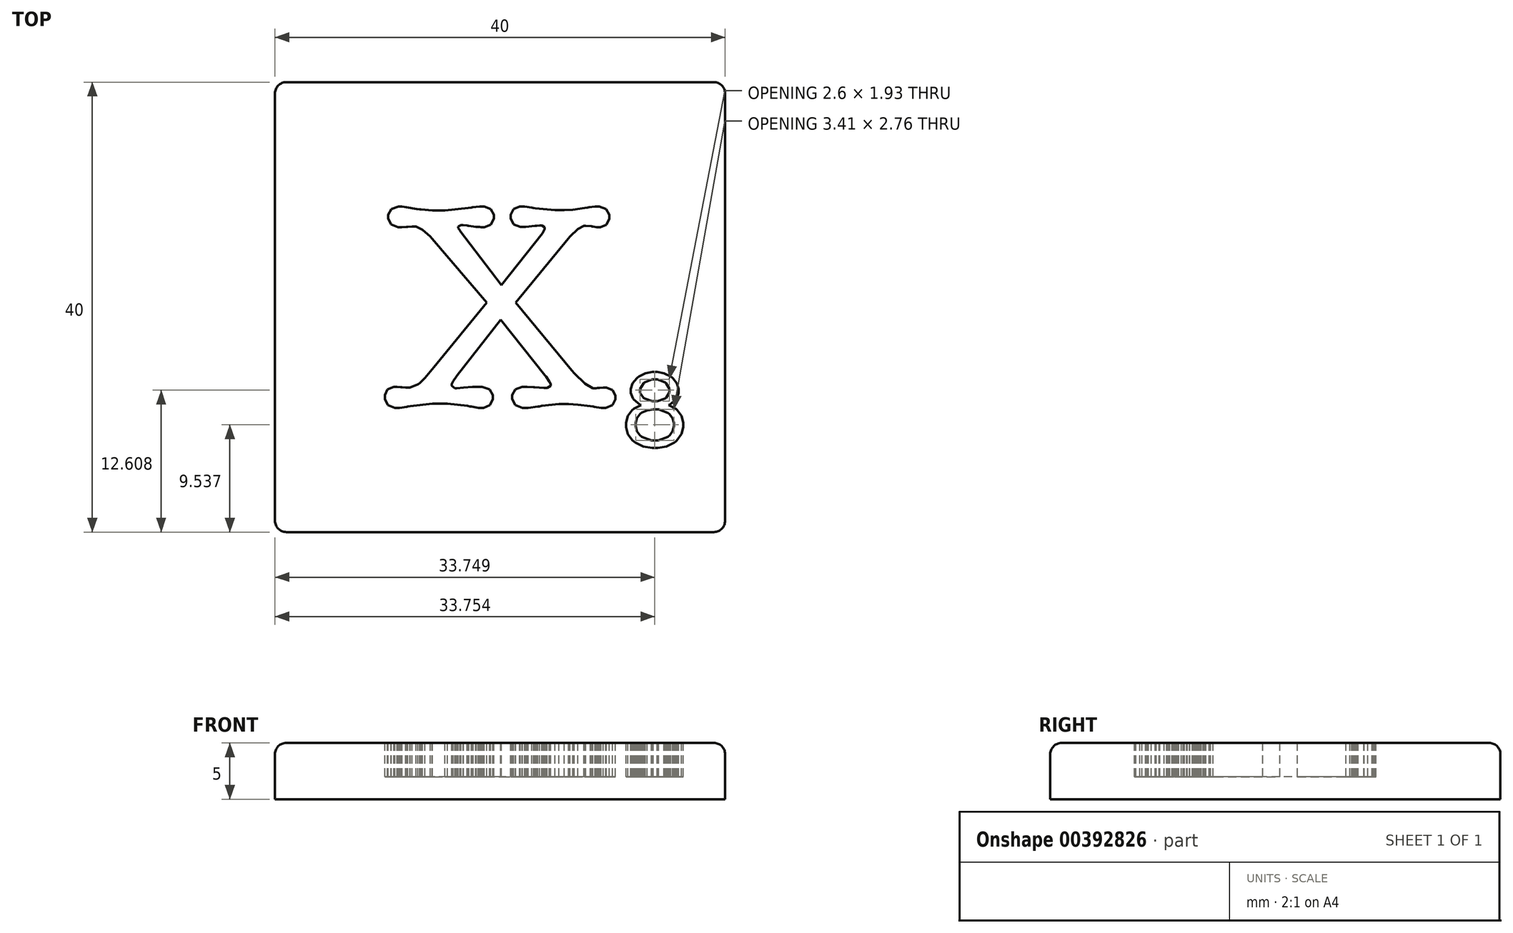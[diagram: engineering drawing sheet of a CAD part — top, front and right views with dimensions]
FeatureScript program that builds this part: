
annotation { "Feature Type Name" : "Feature", "Feature Type Description" : "" }
export const myFeature = defineFeature(function(context is Context, id is Id, definition is map)
    precondition{}
    {
        {
            var Q0;
            Q0=qCreatedBy(makeId("Top.planeOp"),FACE);
            var sketch = newSketch(context, id + "F0", { "sketchPlane" : qUnion([Q0])});
            skLineSegment(sketch, "E0.bottom", {"start": v(20, -20) * mm, "end": v(-20, -20) * mm});
            skLineSegment(sketch, "E0.top", {"start": v(20, 20) * mm, "end": v(-20, 20) * mm});
            skLineSegment(sketch, "E0.left", {"start": v(20, -20) * mm, "end": v(20, 20) * mm});
            skLineSegment(sketch, "E0.right", {"start": v(-20, -20) * mm, "end": v(-20, 20) * mm});
            skPoint(sketch, "E0.middle", {"position": v(0, 0) * mm});
            skSolve(sketch);
        }
        {
            var Q0;
            Q0=makeQuery(id+"F0.imprint","IMPRINT",FACE,{"disambiguationData":[TD([[makeQuery(id+"F0.imprint","IMPRINT",EDGE,{"derivedFrom":sQuery(id+"F0.wireOp",EDGE,"E0.bottom")}),-1.0]])]});
            extrude(context, id + "F1", {"entities" : qUnion([Q0]), "depth" : -5 * mm});
        }
        {
            var Q0;
            Q0=makeQuery(id+"F1.opExtrude","CAP_FACE",FACE,{"disambiguationData":[OSD([sQuery(id+"F0.wireOp",EDGE,"E0.bottom"),sQuery(id+"F0.wireOp",EDGE,"E0.top"),sQuery(id+"F0.wireOp",EDGE,"E0.left"),sQuery(id+"F0.wireOp",EDGE,"E0.right")])],"isStart":true});
            var Q1;
            Q1=makeQuery(id+"F1.opExtrude","SWEPT_EDGE",EDGE,{"disambiguationData":[OSD([sQuery(id+"F0.wireOp",EDGE,"E0.top"),sQuery(id+"F0.wireOp",EDGE,"E0.right")])]});
            var Q2;
            Q2=makeQuery(id+"F1.opExtrude","SWEPT_EDGE",EDGE,{"disambiguationData":[OSD([sQuery(id+"F0.wireOp",EDGE,"E0.top"),sQuery(id+"F0.wireOp",EDGE,"E0.left")])]});
            var Q3;
            Q3=makeQuery(id+"F1.opExtrude","SWEPT_EDGE",EDGE,{"disambiguationData":[OSD([sQuery(id+"F0.wireOp",EDGE,"E0.bottom"),sQuery(id+"F0.wireOp",EDGE,"E0.right")])]});
            var Q4;
            Q4=makeQuery(id+"F1.opExtrude","SWEPT_EDGE",EDGE,{"disambiguationData":[OSD([sQuery(id+"F0.wireOp",EDGE,"E0.bottom"),sQuery(id+"F0.wireOp",EDGE,"E0.left")])]});
            fillet(context, id + "F2", {"entities" : qUnion([Q0, Q1, Q2, Q3, Q4]), "radius" : 1 * mm, "tangentPropagation" : true, "allowEdgeOverflow" : false});
        }
        {
            var Q0;
            Q0=qCreatedBy(makeId("Top.planeOp"),FACE);
            var sketch = newSketch(context, id + "F3", { "sketchPlane" : qUnion([Q0])});
            skLineSegment(sketch, "E1", {"start": v(-5.87, -5.36) * mm, "end": v(-1.2, 0.41) * mm});
            skLineSegment(sketch, "E2", {"start": v(-1.2, 0.41) * mm, "end": v(-6.03, 6.1) * mm});
            skLineSegment(sketch, "E3", {"start": v(-6.03, 6.1) * mm, "end": v(-6.18, 6.28) * mm});
            skLineSegment(sketch, "E4", {"start": v(-6.18, 6.28) * mm, "end": v(-6.9, 6.9) * mm});
            skLineSegment(sketch, "E5", {"start": v(-6.9, 6.9) * mm, "end": v(-7.48, 7.16) * mm});
            skLineSegment(sketch, "E6", {"start": v(-7.48, 7.16) * mm, "end": v(-7.67, 7.16) * mm});
            skLineSegment(sketch, "E7", {"start": v(-7.67, 7.16) * mm, "end": v(-7.82, 7.16) * mm});
            skLineSegment(sketch, "E8", {"start": v(-7.82, 7.16) * mm, "end": v(-8.2, 7.14) * mm});
            skLineSegment(sketch, "E9", {"start": v(-8.2, 7.14) * mm, "end": v(-8.27, 7.13) * mm});
            skLineSegment(sketch, "E10", {"start": v(-8.27, 7.13) * mm, "end": v(-8.33, 7.13) * mm});
            skLineSegment(sketch, "E11", {"start": v(-8.33, 7.13) * mm, "end": v(-8.73, 7.1) * mm});
            skLineSegment(sketch, "E12", {"start": v(-8.73, 7.1) * mm, "end": v(-8.86, 7.1) * mm});
            skLineSegment(sketch, "E13", {"start": v(-8.86, 7.1) * mm, "end": v(-9.07, 7.1) * mm});
            skLineSegment(sketch, "E14", {"start": v(-9.07, 7.1) * mm, "end": v(-9.68, 7.34) * mm});
            skLineSegment(sketch, "E15", {"start": v(-9.68, 7.34) * mm, "end": v(-9.95, 7.88) * mm});
            skLineSegment(sketch, "E16", {"start": v(-9.95, 7.88) * mm, "end": v(-9.95, 8.06) * mm});
            skLineSegment(sketch, "E17", {"start": v(-9.95, 8.06) * mm, "end": v(-9.95, 8.23) * mm});
            skLineSegment(sketch, "E18", {"start": v(-9.95, 8.23) * mm, "end": v(-9.66, 8.73) * mm});
            skLineSegment(sketch, "E19", {"start": v(-9.66, 8.73) * mm, "end": v(-9.02, 8.96) * mm});
            skLineSegment(sketch, "E20", {"start": v(-9.02, 8.96) * mm, "end": v(-8.81, 8.96) * mm});
            skLineSegment(sketch, "E21", {"start": v(-8.81, 8.96) * mm, "end": v(-8.7, 8.96) * mm});
            skLineSegment(sketch, "E22", {"start": v(-8.7, 8.96) * mm, "end": v(-8.33, 8.89) * mm});
            skLineSegment(sketch, "E23", {"start": v(-8.33, 8.89) * mm, "end": v(-7.4, 8.74) * mm});
            skLineSegment(sketch, "E24", {"start": v(-7.4, 8.74) * mm, "end": v(-7.14, 8.7) * mm});
            skLineSegment(sketch, "E25", {"start": v(-7.14, 8.7) * mm, "end": v(-7.02, 8.67) * mm});
            skLineSegment(sketch, "E26", {"start": v(-7.02, 8.67) * mm, "end": v(-6, 8.59) * mm});
            skLineSegment(sketch, "E27", {"start": v(-6, 8.59) * mm, "end": v(-5.66, 8.59) * mm});
            skLineSegment(sketch, "E28", {"start": v(-5.66, 8.59) * mm, "end": v(-4.88, 8.59) * mm});
            skLineSegment(sketch, "E29", {"start": v(-4.88, 8.59) * mm, "end": v(-2.83, 8.8) * mm});
            skLineSegment(sketch, "E30", {"start": v(-2.83, 8.8) * mm, "end": v(-2.54, 8.85) * mm});
            skLineSegment(sketch, "E31", {"start": v(-2.54, 8.85) * mm, "end": v(-2.45, 8.86) * mm});
            skLineSegment(sketch, "E32", {"start": v(-2.45, 8.86) * mm, "end": v(-1.82, 8.93) * mm});
            skLineSegment(sketch, "E33", {"start": v(-1.82, 8.93) * mm, "end": v(-1.61, 8.93) * mm});
            skLineSegment(sketch, "E34", {"start": v(-1.61, 8.93) * mm, "end": v(-1.42, 8.93) * mm});
            skLineSegment(sketch, "E35", {"start": v(-1.42, 8.93) * mm, "end": v(-0.82, 8.7) * mm});
            skLineSegment(sketch, "E36", {"start": v(-0.82, 8.7) * mm, "end": v(-0.56, 8.2) * mm});
            skLineSegment(sketch, "E37", {"start": v(-0.56, 8.2) * mm, "end": v(-0.56, 8.03) * mm});
            skLineSegment(sketch, "E38", {"start": v(-0.56, 8.03) * mm, "end": v(-0.56, 7.86) * mm});
            skLineSegment(sketch, "E39", {"start": v(-0.56, 7.86) * mm, "end": v(-0.82, 7.34) * mm});
            skLineSegment(sketch, "E40", {"start": v(-0.82, 7.34) * mm, "end": v(-1.42, 7.1) * mm});
            skLineSegment(sketch, "E41", {"start": v(-1.42, 7.1) * mm, "end": v(-1.61, 7.1) * mm});
            skLineSegment(sketch, "E42", {"start": v(-1.61, 7.1) * mm, "end": v(-1.68, 7.1) * mm});
            skLineSegment(sketch, "E43", {"start": v(-1.68, 7.1) * mm, "end": v(-1.83, 7.13) * mm});
            skLineSegment(sketch, "E44", {"start": v(-1.83, 7.13) * mm, "end": v(-1.85, 7.13) * mm});
            skLineSegment(sketch, "E45", {"start": v(-1.85, 7.13) * mm, "end": v(-2.1, 7.13) * mm});
            skLineSegment(sketch, "E46", {"start": v(-2.1, 7.13) * mm, "end": v(-2.15, 7.14) * mm});
            skLineSegment(sketch, "E47", {"start": v(-2.15, 7.14) * mm, "end": v(-2.78, 7.23) * mm});
            skLineSegment(sketch, "E48", {"start": v(-2.78, 7.23) * mm, "end": v(-2.84, 7.24) * mm});
            skLineSegment(sketch, "E49", {"start": v(-2.84, 7.24) * mm, "end": v(-2.91, 7.25) * mm});
            skLineSegment(sketch, "E50", {"start": v(-2.91, 7.25) * mm, "end": v(-3.27, 7.29) * mm});
            skLineSegment(sketch, "E51", {"start": v(-3.27, 7.29) * mm, "end": v(-3.39, 7.29) * mm});
            skLineSegment(sketch, "E52", {"start": v(-3.39, 7.29) * mm, "end": v(-3.47, 7.29) * mm});
            skLineSegment(sketch, "E53", {"start": v(-3.47, 7.29) * mm, "end": v(-3.7, 7.15) * mm});
            skLineSegment(sketch, "E54", {"start": v(-3.7, 7.15) * mm, "end": v(-3.7, 7.1) * mm});
            skLineSegment(sketch, "E55", {"start": v(-3.7, 7.1) * mm, "end": v(-3.7, 7.03) * mm});
            skLineSegment(sketch, "E56", {"start": v(-3.7, 7.03) * mm, "end": v(-3.57, 6.82) * mm});
            skLineSegment(sketch, "E57", {"start": v(-3.57, 6.82) * mm, "end": v(-3.55, 6.79) * mm});
            skLineSegment(sketch, "E58", {"start": v(-3.55, 6.79) * mm, "end": v(0.13, 1.97) * mm});
            skLineSegment(sketch, "E59", {"start": v(0.13, 1.97) * mm, "end": v(3.76, 6.57) * mm});
            skLineSegment(sketch, "E60", {"start": v(3.76, 6.57) * mm, "end": v(3.8, 6.62) * mm});
            skLineSegment(sketch, "E61", {"start": v(3.8, 6.62) * mm, "end": v(3.97, 6.94) * mm});
            skLineSegment(sketch, "E62", {"start": v(3.97, 6.94) * mm, "end": v(3.97, 7.05) * mm});
            skLineSegment(sketch, "E63", {"start": v(3.97, 7.05) * mm, "end": v(3.97, 7.1) * mm});
            skLineSegment(sketch, "E64", {"start": v(3.97, 7.1) * mm, "end": v(3.71, 7.26) * mm});
            skLineSegment(sketch, "E65", {"start": v(3.71, 7.26) * mm, "end": v(3.62, 7.26) * mm});
            skLineSegment(sketch, "E66", {"start": v(3.62, 7.26) * mm, "end": v(3.53, 7.26) * mm});
            skLineSegment(sketch, "E67", {"start": v(3.53, 7.26) * mm, "end": v(3.26, 7.24) * mm});
            skLineSegment(sketch, "E68", {"start": v(3.26, 7.24) * mm, "end": v(3.23, 7.24) * mm});
            skLineSegment(sketch, "E69", {"start": v(3.23, 7.24) * mm, "end": v(3.1, 7.22) * mm});
            skLineSegment(sketch, "E70", {"start": v(3.1, 7.22) * mm, "end": v(2.28, 7.13) * mm});
            skLineSegment(sketch, "E71", {"start": v(2.28, 7.13) * mm, "end": v(2, 7.13) * mm});
            skLineSegment(sketch, "E72", {"start": v(2, 7.13) * mm, "end": v(1.81, 7.13) * mm});
            skLineSegment(sketch, "E73", {"start": v(1.81, 7.13) * mm, "end": v(1.22, 7.36) * mm});
            skLineSegment(sketch, "E74", {"start": v(1.22, 7.36) * mm, "end": v(0.95, 7.88) * mm});
            skLineSegment(sketch, "E75", {"start": v(0.95, 7.88) * mm, "end": v(0.95, 8.06) * mm});
            skLineSegment(sketch, "E76", {"start": v(0.95, 8.06) * mm, "end": v(0.95, 8.22) * mm});
            skLineSegment(sketch, "E77", {"start": v(0.95, 8.22) * mm, "end": v(1.2, 8.71) * mm});
            skLineSegment(sketch, "E78", {"start": v(1.2, 8.71) * mm, "end": v(1.75, 8.93) * mm});
            skLineSegment(sketch, "E79", {"start": v(1.75, 8.93) * mm, "end": v(1.93, 8.93) * mm});
            skLineSegment(sketch, "E80", {"start": v(1.93, 8.93) * mm, "end": v(2.18, 8.93) * mm});
            skLineSegment(sketch, "E81", {"start": v(2.18, 8.93) * mm, "end": v(2.83, 8.84) * mm});
            skLineSegment(sketch, "E82", {"start": v(2.83, 8.84) * mm, "end": v(2.94, 8.82) * mm});
            skLineSegment(sketch, "E83", {"start": v(2.94, 8.82) * mm, "end": v(3.14, 8.79) * mm});
            skLineSegment(sketch, "E84", {"start": v(3.14, 8.79) * mm, "end": v(4.9, 8.61) * mm});
            skLineSegment(sketch, "E85", {"start": v(4.9, 8.61) * mm, "end": v(5.48, 8.61) * mm});
            skLineSegment(sketch, "E86", {"start": v(5.48, 8.61) * mm, "end": v(5.72, 8.61) * mm});
            skLineSegment(sketch, "E87", {"start": v(5.72, 8.61) * mm, "end": v(6.46, 8.67) * mm});
            skLineSegment(sketch, "E88", {"start": v(6.46, 8.67) * mm, "end": v(7.53, 8.81) * mm});
            skLineSegment(sketch, "E89", {"start": v(7.53, 8.81) * mm, "end": v(7.78, 8.85) * mm});
            skLineSegment(sketch, "E90", {"start": v(7.78, 8.85) * mm, "end": v(7.89, 8.87) * mm});
            skLineSegment(sketch, "E91", {"start": v(7.89, 8.87) * mm, "end": v(8.44, 8.96) * mm});
            skLineSegment(sketch, "E92", {"start": v(8.44, 8.96) * mm, "end": v(8.62, 8.96) * mm});
            skLineSegment(sketch, "E93", {"start": v(8.62, 8.96) * mm, "end": v(8.83, 8.96) * mm});
            skLineSegment(sketch, "E94", {"start": v(8.83, 8.96) * mm, "end": v(9.44, 8.72) * mm});
            skLineSegment(sketch, "E95", {"start": v(9.44, 8.72) * mm, "end": v(9.71, 8.2) * mm});
            skLineSegment(sketch, "E96", {"start": v(9.71, 8.2) * mm, "end": v(9.71, 8.03) * mm});
            skLineSegment(sketch, "E97", {"start": v(9.71, 8.03) * mm, "end": v(9.71, 7.86) * mm});
            skLineSegment(sketch, "E98", {"start": v(9.71, 7.86) * mm, "end": v(9.47, 7.34) * mm});
            skLineSegment(sketch, "E99", {"start": v(9.47, 7.34) * mm, "end": v(8.91, 7.1) * mm});
            skLineSegment(sketch, "E100", {"start": v(8.91, 7.1) * mm, "end": v(8.73, 7.1) * mm});
            skLineSegment(sketch, "E101", {"start": v(8.73, 7.1) * mm, "end": v(8.6, 7.1) * mm});
            skLineSegment(sketch, "E102", {"start": v(8.6, 7.1) * mm, "end": v(8.24, 7.16) * mm});
            skLineSegment(sketch, "E103", {"start": v(8.24, 7.16) * mm, "end": v(8.18, 7.17) * mm});
            skLineSegment(sketch, "E104", {"start": v(8.18, 7.17) * mm, "end": v(8.11, 7.18) * mm});
            skLineSegment(sketch, "E105", {"start": v(8.11, 7.18) * mm, "end": v(7.62, 7.24) * mm});
            skLineSegment(sketch, "E106", {"start": v(7.62, 7.24) * mm, "end": v(7.44, 7.24) * mm});
            skLineSegment(sketch, "E107", {"start": v(7.44, 7.24) * mm, "end": v(6.91, 6.95) * mm});
            skLineSegment(sketch, "E108", {"start": v(6.91, 6.95) * mm, "end": v(6.21, 6.29) * mm});
            skLineSegment(sketch, "E109", {"start": v(6.21, 6.29) * mm, "end": v(6.06, 6.1) * mm});
            skLineSegment(sketch, "E110", {"start": v(6.06, 6.1) * mm, "end": v(1.4, 0.41) * mm});
            skLineSegment(sketch, "E111", {"start": v(1.4, 0.41) * mm, "end": v(6.38, -5.62) * mm});
            skLineSegment(sketch, "E112", {"start": v(6.38, -5.62) * mm, "end": v(6.6, -5.89) * mm});
            skLineSegment(sketch, "E113", {"start": v(6.6, -5.89) * mm, "end": v(7.55, -6.81) * mm});
            skLineSegment(sketch, "E114", {"start": v(7.55, -6.81) * mm, "end": v(8.26, -7.2) * mm});
            skLineSegment(sketch, "E115", {"start": v(8.26, -7.2) * mm, "end": v(8.5, -7.2) * mm});
            skLineSegment(sketch, "E116", {"start": v(8.5, -7.2) * mm, "end": v(8.54, -7.2) * mm});
            skLineSegment(sketch, "E117", {"start": v(8.54, -7.2) * mm, "end": v(8.66, -7.19) * mm});
            skLineSegment(sketch, "E118", {"start": v(8.66, -7.19) * mm, "end": v(8.68, -7.18) * mm});
            skLineSegment(sketch, "E119", {"start": v(8.68, -7.18) * mm, "end": v(8.84, -7.18) * mm});
            skLineSegment(sketch, "E120", {"start": v(8.84, -7.18) * mm, "end": v(8.86, -7.18) * mm});
            skLineSegment(sketch, "E121", {"start": v(8.86, -7.18) * mm, "end": v(9.16, -7.16) * mm});
            skLineSegment(sketch, "E122", {"start": v(9.16, -7.16) * mm, "end": v(9.26, -7.16) * mm});
            skLineSegment(sketch, "E123", {"start": v(9.26, -7.16) * mm, "end": v(9.44, -7.16) * mm});
            skLineSegment(sketch, "E124", {"start": v(9.44, -7.16) * mm, "end": v(10, -7.37) * mm});
            skLineSegment(sketch, "E125", {"start": v(10, -7.37) * mm, "end": v(10.24, -7.87) * mm});
            skLineSegment(sketch, "E126", {"start": v(10.24, -7.87) * mm, "end": v(10.24, -8.03) * mm});
            skLineSegment(sketch, "E127", {"start": v(10.24, -8.03) * mm, "end": v(10.24, -8.2) * mm});
            skLineSegment(sketch, "E128", {"start": v(10.24, -8.2) * mm, "end": v(9.98, -8.72) * mm});
            skLineSegment(sketch, "E129", {"start": v(9.98, -8.72) * mm, "end": v(9.4, -8.96) * mm});
            skLineSegment(sketch, "E130", {"start": v(9.4, -8.96) * mm, "end": v(9.2, -8.96) * mm});
            skLineSegment(sketch, "E131", {"start": v(9.2, -8.96) * mm, "end": v(8.98, -8.96) * mm});
            skLineSegment(sketch, "E132", {"start": v(8.98, -8.96) * mm, "end": v(8.4, -8.87) * mm});
            skLineSegment(sketch, "E133", {"start": v(8.4, -8.87) * mm, "end": v(8.28, -8.85) * mm});
            skLineSegment(sketch, "E134", {"start": v(8.28, -8.85) * mm, "end": v(8.03, -8.8) * mm});
            skLineSegment(sketch, "E135", {"start": v(8.03, -8.8) * mm, "end": v(6.91, -8.67) * mm});
            skLineSegment(sketch, "E136", {"start": v(6.91, -8.67) * mm, "end": v(6.1, -8.61) * mm});
            skLineSegment(sketch, "E137", {"start": v(6.1, -8.61) * mm, "end": v(5.82, -8.61) * mm});
            skLineSegment(sketch, "E138", {"start": v(5.82, -8.61) * mm, "end": v(5.24, -8.61) * mm});
            skLineSegment(sketch, "E139", {"start": v(5.24, -8.61) * mm, "end": v(3.7, -8.79) * mm});
            skLineSegment(sketch, "E140", {"start": v(3.7, -8.79) * mm, "end": v(3.5, -8.82) * mm});
            skLineSegment(sketch, "E141", {"start": v(3.5, -8.82) * mm, "end": v(3.36, -8.85) * mm});
            skLineSegment(sketch, "E142", {"start": v(3.36, -8.85) * mm, "end": v(2.5, -8.96) * mm});
            skLineSegment(sketch, "E143", {"start": v(2.5, -8.96) * mm, "end": v(2.22, -8.96) * mm});
            skLineSegment(sketch, "E144", {"start": v(2.22, -8.96) * mm, "end": v(2, -8.96) * mm});
            skLineSegment(sketch, "E145", {"start": v(2, -8.96) * mm, "end": v(1.37, -8.72) * mm});
            skLineSegment(sketch, "E146", {"start": v(1.37, -8.72) * mm, "end": v(1.08, -8.18) * mm});
            skLineSegment(sketch, "E147", {"start": v(1.08, -8.18) * mm, "end": v(1.08, -8) * mm});
            skLineSegment(sketch, "E148", {"start": v(1.08, -8) * mm, "end": v(1.08, -7.83) * mm});
            skLineSegment(sketch, "E149", {"start": v(1.08, -7.83) * mm, "end": v(1.36, -7.33) * mm});
            skLineSegment(sketch, "E150", {"start": v(1.36, -7.33) * mm, "end": v(1.97, -7.1) * mm});
            skLineSegment(sketch, "E151", {"start": v(1.97, -7.1) * mm, "end": v(2.17, -7.1) * mm});
            skLineSegment(sketch, "E152", {"start": v(2.17, -7.1) * mm, "end": v(2.4, -7.1) * mm});
            skLineSegment(sketch, "E153", {"start": v(2.4, -7.1) * mm, "end": v(3, -7.12) * mm});
            skLineSegment(sketch, "E154", {"start": v(3, -7.12) * mm, "end": v(3.07, -7.13) * mm});
            skLineSegment(sketch, "E155", {"start": v(3.07, -7.13) * mm, "end": v(3.89, -7.18) * mm});
            skLineSegment(sketch, "E156", {"start": v(3.89, -7.18) * mm, "end": v(4.07, -7.18) * mm});
            skLineSegment(sketch, "E157", {"start": v(4.07, -7.18) * mm, "end": v(4.18, -7.18) * mm});
            skLineSegment(sketch, "E158", {"start": v(4.18, -7.18) * mm, "end": v(4.5, -6.99) * mm});
            skLineSegment(sketch, "E159", {"start": v(4.5, -6.99) * mm, "end": v(4.5, -6.92) * mm});
            skLineSegment(sketch, "E160", {"start": v(4.5, -6.92) * mm, "end": v(4.5, -6.84) * mm});
            skLineSegment(sketch, "E161", {"start": v(4.5, -6.84) * mm, "end": v(4.37, -6.6) * mm});
            skLineSegment(sketch, "E162", {"start": v(4.37, -6.6) * mm, "end": v(4.08, -6.18) * mm});
            skLineSegment(sketch, "E163", {"start": v(4.08, -6.18) * mm, "end": v(4, -6.07) * mm});
            skLineSegment(sketch, "E164", {"start": v(4, -6.07) * mm, "end": v(0.05, -1.12) * mm});
            skLineSegment(sketch, "E165", {"start": v(0.05, -1.12) * mm, "end": v(-3.81, -6.07) * mm});
            skLineSegment(sketch, "E166", {"start": v(-3.81, -6.07) * mm, "end": v(-3.9, -6.17) * mm});
            skLineSegment(sketch, "E167", {"start": v(-3.9, -6.17) * mm, "end": v(-4.17, -6.59) * mm});
            skLineSegment(sketch, "E168", {"start": v(-4.17, -6.59) * mm, "end": v(-4.29, -6.84) * mm});
            skLineSegment(sketch, "E169", {"start": v(-4.29, -6.84) * mm, "end": v(-4.29, -6.92) * mm});
            skLineSegment(sketch, "E170", {"start": v(-4.29, -6.92) * mm, "end": v(-4.29, -7) * mm});
            skLineSegment(sketch, "E171", {"start": v(-4.29, -7) * mm, "end": v(-4, -7.2) * mm});
            skLineSegment(sketch, "E172", {"start": v(-4, -7.2) * mm, "end": v(-3.92, -7.2) * mm});
            skLineSegment(sketch, "E173", {"start": v(-3.92, -7.2) * mm, "end": v(-3.86, -7.2) * mm});
            skLineSegment(sketch, "E174", {"start": v(-3.86, -7.2) * mm, "end": v(-3.25, -7.16) * mm});
            skLineSegment(sketch, "E175", {"start": v(-3.25, -7.16) * mm, "end": v(-2.46, -7.1) * mm});
            skLineSegment(sketch, "E176", {"start": v(-2.46, -7.1) * mm, "end": v(-2.4, -7.1) * mm});
            skLineSegment(sketch, "E177", {"start": v(-2.4, -7.1) * mm, "end": v(-1.95, -7.08) * mm});
            skLineSegment(sketch, "E178", {"start": v(-1.95, -7.08) * mm, "end": v(-1.8, -7.08) * mm});
            skLineSegment(sketch, "E179", {"start": v(-1.8, -7.08) * mm, "end": v(-1.58, -7.08) * mm});
            skLineSegment(sketch, "E180", {"start": v(-1.58, -7.08) * mm, "end": v(-0.93, -7.3) * mm});
            skLineSegment(sketch, "E181", {"start": v(-0.93, -7.3) * mm, "end": v(-0.64, -7.83) * mm});
            skLineSegment(sketch, "E182", {"start": v(-0.64, -7.83) * mm, "end": v(-0.64, -8) * mm});
            skLineSegment(sketch, "E183", {"start": v(-0.64, -8) * mm, "end": v(-0.64, -8.18) * mm});
            skLineSegment(sketch, "E184", {"start": v(-0.64, -8.18) * mm, "end": v(-0.89, -8.72) * mm});
            skLineSegment(sketch, "E185", {"start": v(-0.89, -8.72) * mm, "end": v(-1.45, -8.96) * mm});
            skLineSegment(sketch, "E186", {"start": v(-1.45, -8.96) * mm, "end": v(-1.64, -8.96) * mm});
            skLineSegment(sketch, "E187", {"start": v(-1.64, -8.96) * mm, "end": v(-1.9, -8.96) * mm});
            skLineSegment(sketch, "E188", {"start": v(-1.9, -8.96) * mm, "end": v(-2.55, -8.85) * mm});
            skLineSegment(sketch, "E189", {"start": v(-2.55, -8.85) * mm, "end": v(-2.67, -8.82) * mm});
            skLineSegment(sketch, "E190", {"start": v(-2.67, -8.82) * mm, "end": v(-2.89, -8.78) * mm});
            skLineSegment(sketch, "E191", {"start": v(-2.89, -8.78) * mm, "end": v(-4.67, -8.59) * mm});
            skLineSegment(sketch, "E192", {"start": v(-4.67, -8.59) * mm, "end": v(-5.27, -8.59) * mm});
            skLineSegment(sketch, "E193", {"start": v(-5.27, -8.59) * mm, "end": v(-6, -8.59) * mm});
            skLineSegment(sketch, "E194", {"start": v(-6, -8.59) * mm, "end": v(-7.96, -8.8) * mm});
            skLineSegment(sketch, "E195", {"start": v(-7.96, -8.8) * mm, "end": v(-8.2, -8.85) * mm});
            skLineSegment(sketch, "E196", {"start": v(-8.2, -8.85) * mm, "end": v(-8.3, -8.87) * mm});
            skLineSegment(sketch, "E197", {"start": v(-8.3, -8.87) * mm, "end": v(-8.92, -8.96) * mm});
            skLineSegment(sketch, "E198", {"start": v(-8.92, -8.96) * mm, "end": v(-9.13, -8.96) * mm});
            skLineSegment(sketch, "E199", {"start": v(-9.13, -8.96) * mm, "end": v(-9.34, -8.96) * mm});
            skLineSegment(sketch, "E200", {"start": v(-9.34, -8.96) * mm, "end": v(-9.96, -8.72) * mm});
            skLineSegment(sketch, "E201", {"start": v(-9.96, -8.72) * mm, "end": v(-10.24, -8.18) * mm});
            skLineSegment(sketch, "E202", {"start": v(-10.24, -8.18) * mm, "end": v(-10.24, -8) * mm});
            skLineSegment(sketch, "E203", {"start": v(-10.24, -8) * mm, "end": v(-10.24, -7.83) * mm});
            skLineSegment(sketch, "E204", {"start": v(-10.24, -7.83) * mm, "end": v(-10, -7.3) * mm});
            skLineSegment(sketch, "E205", {"start": v(-10, -7.3) * mm, "end": v(-9.45, -7.08) * mm});
            skLineSegment(sketch, "E206", {"start": v(-9.45, -7.08) * mm, "end": v(-9.26, -7.08) * mm});
            skLineSegment(sketch, "E207", {"start": v(-9.26, -7.08) * mm, "end": v(-9.14, -7.08) * mm});
            skLineSegment(sketch, "E208", {"start": v(-9.14, -7.08) * mm, "end": v(-8.83, -7.11) * mm});
            skLineSegment(sketch, "E209", {"start": v(-8.83, -7.11) * mm, "end": v(-8.77, -7.12) * mm});
            skLineSegment(sketch, "E210", {"start": v(-8.77, -7.12) * mm, "end": v(-8.72, -7.12) * mm});
            skLineSegment(sketch, "E211", {"start": v(-8.72, -7.12) * mm, "end": v(-8.4, -7.16) * mm});
            skLineSegment(sketch, "E212", {"start": v(-8.4, -7.16) * mm, "end": v(-8.28, -7.16) * mm});
            skLineSegment(sketch, "E213", {"start": v(-8.28, -7.16) * mm, "end": v(-8.02, -7.16) * mm});
            skLineSegment(sketch, "E214", {"start": v(-8.02, -7.16) * mm, "end": v(-7.3, -6.88) * mm});
            skLineSegment(sketch, "E215", {"start": v(-7.3, -6.88) * mm, "end": v(-7.24, -6.83) * mm});
            skLineSegment(sketch, "E216", {"start": v(-7.24, -6.83) * mm, "end": v(-7.17, -6.77) * mm});
            skLineSegment(sketch, "E217", {"start": v(-7.17, -6.77) * mm, "end": v(-6.68, -6.3) * mm});
            skLineSegment(sketch, "E218", {"start": v(-6.68, -6.3) * mm, "end": v(-6.03, -5.55) * mm});
            skLineSegment(sketch, "E219", {"start": v(-6.03, -5.55) * mm, "end": v(-5.87, -5.36) * mm});
            skSolve(sketch);
        }
        {
            var Q0;
            Q0=qCreatedBy(makeId("Top.planeOp"),FACE);
            var sketch = newSketch(context, id + "F4", { "sketchPlane" : qUnion([Q0])});
            skLineSegment(sketch, "E220", {"start": v(11.87, -9.06) * mm, "end": v(11.9, -9.03) * mm});
            skLineSegment(sketch, "E221", {"start": v(11.9, -9.03) * mm, "end": v(12.46, -8.74) * mm});
            skLineSegment(sketch, "E222", {"start": v(12.46, -8.74) * mm, "end": v(12.53, -8.72) * mm});
            skLineSegment(sketch, "E223", {"start": v(12.53, -8.72) * mm, "end": v(12.45, -8.67) * mm});
            skLineSegment(sketch, "E224", {"start": v(12.45, -8.67) * mm, "end": v(11.85, -8.2) * mm});
            skLineSegment(sketch, "E225", {"start": v(11.85, -8.2) * mm, "end": v(11.82, -8.15) * mm});
            skLineSegment(sketch, "E226", {"start": v(11.82, -8.15) * mm, "end": v(11.79, -8.1) * mm});
            skLineSegment(sketch, "E227", {"start": v(11.79, -8.1) * mm, "end": v(11.63, -7.62) * mm});
            skLineSegment(sketch, "E228", {"start": v(11.63, -7.62) * mm, "end": v(11.63, -7.45) * mm});
            skLineSegment(sketch, "E229", {"start": v(11.63, -7.45) * mm, "end": v(11.63, -7.29) * mm});
            skLineSegment(sketch, "E230", {"start": v(11.63, -7.29) * mm, "end": v(11.78, -6.79) * mm});
            skLineSegment(sketch, "E231", {"start": v(11.78, -6.79) * mm, "end": v(12.14, -6.32) * mm});
            skLineSegment(sketch, "E232", {"start": v(12.14, -6.32) * mm, "end": v(12.24, -6.24) * mm});
            skLineSegment(sketch, "E233", {"start": v(12.24, -6.24) * mm, "end": v(12.35, -6.16) * mm});
            skLineSegment(sketch, "E234", {"start": v(12.35, -6.16) * mm, "end": v(12.93, -5.87) * mm});
            skLineSegment(sketch, "E235", {"start": v(12.93, -5.87) * mm, "end": v(13.55, -5.75) * mm});
            skLineSegment(sketch, "E236", {"start": v(13.55, -5.75) * mm, "end": v(13.75, -5.75) * mm});
            skLineSegment(sketch, "E237", {"start": v(13.75, -5.75) * mm, "end": v(13.96, -5.75) * mm});
            skLineSegment(sketch, "E238", {"start": v(13.96, -5.75) * mm, "end": v(14.58, -5.87) * mm});
            skLineSegment(sketch, "E239", {"start": v(14.58, -5.87) * mm, "end": v(15.16, -6.16) * mm});
            skLineSegment(sketch, "E240", {"start": v(15.16, -6.16) * mm, "end": v(15.26, -6.24) * mm});
            skLineSegment(sketch, "E241", {"start": v(15.26, -6.24) * mm, "end": v(15.37, -6.32) * mm});
            skLineSegment(sketch, "E242", {"start": v(15.37, -6.32) * mm, "end": v(15.72, -6.79) * mm});
            skLineSegment(sketch, "E243", {"start": v(15.72, -6.79) * mm, "end": v(15.88, -7.29) * mm});
            skLineSegment(sketch, "E244", {"start": v(15.88, -7.29) * mm, "end": v(15.88, -7.45) * mm});
            skLineSegment(sketch, "E245", {"start": v(15.88, -7.45) * mm, "end": v(15.88, -7.63) * mm});
            skLineSegment(sketch, "E246", {"start": v(15.88, -7.63) * mm, "end": v(15.72, -8.1) * mm});
            skLineSegment(sketch, "E247", {"start": v(15.72, -8.1) * mm, "end": v(15.68, -8.15) * mm});
            skLineSegment(sketch, "E248", {"start": v(15.68, -8.15) * mm, "end": v(15.65, -8.2) * mm});
            skLineSegment(sketch, "E249", {"start": v(15.65, -8.2) * mm, "end": v(15.06, -8.67) * mm});
            skLineSegment(sketch, "E250", {"start": v(15.06, -8.67) * mm, "end": v(14.97, -8.72) * mm});
            skLineSegment(sketch, "E251", {"start": v(14.97, -8.72) * mm, "end": v(15.04, -8.74) * mm});
            skLineSegment(sketch, "E252", {"start": v(15.04, -8.74) * mm, "end": v(15.59, -9.03) * mm});
            skLineSegment(sketch, "E253", {"start": v(15.59, -9.03) * mm, "end": v(15.63, -9.06) * mm});
            skLineSegment(sketch, "E254", {"start": v(15.63, -9.06) * mm, "end": v(15.74, -9.15) * mm});
            skLineSegment(sketch, "E255", {"start": v(15.74, -9.15) * mm, "end": v(16.13, -9.67) * mm});
            skLineSegment(sketch, "E256", {"start": v(16.13, -9.67) * mm, "end": v(16.3, -10.26) * mm});
            skLineSegment(sketch, "E257", {"start": v(16.3, -10.26) * mm, "end": v(16.3, -10.46) * mm});
            skLineSegment(sketch, "E258", {"start": v(16.3, -10.46) * mm, "end": v(16.3, -10.67) * mm});
            skLineSegment(sketch, "E259", {"start": v(16.3, -10.67) * mm, "end": v(16.12, -11.3) * mm});
            skLineSegment(sketch, "E260", {"start": v(16.12, -11.3) * mm, "end": v(15.72, -11.85) * mm});
            skLineSegment(sketch, "E261", {"start": v(15.72, -11.85) * mm, "end": v(15.6, -11.95) * mm});
            skLineSegment(sketch, "E262", {"start": v(15.6, -11.95) * mm, "end": v(15.49, -12.04) * mm});
            skLineSegment(sketch, "E263", {"start": v(15.49, -12.04) * mm, "end": v(14.8, -12.38) * mm});
            skLineSegment(sketch, "E264", {"start": v(14.8, -12.38) * mm, "end": v(14.04, -12.52) * mm});
            skLineSegment(sketch, "E265", {"start": v(14.04, -12.52) * mm, "end": v(13.78, -12.52) * mm});
            skLineSegment(sketch, "E266", {"start": v(13.78, -12.52) * mm, "end": v(13.52, -12.52) * mm});
            skLineSegment(sketch, "E267", {"start": v(13.52, -12.52) * mm, "end": v(12.73, -12.38) * mm});
            skLineSegment(sketch, "E268", {"start": v(12.73, -12.38) * mm, "end": v(12.02, -12.05) * mm});
            skLineSegment(sketch, "E269", {"start": v(12.02, -12.05) * mm, "end": v(11.9, -11.96) * mm});
            skLineSegment(sketch, "E270", {"start": v(11.9, -11.96) * mm, "end": v(11.79, -11.86) * mm});
            skLineSegment(sketch, "E271", {"start": v(11.79, -11.86) * mm, "end": v(11.38, -11.3) * mm});
            skLineSegment(sketch, "E272", {"start": v(11.38, -11.3) * mm, "end": v(11.2, -10.67) * mm});
            skLineSegment(sketch, "E273", {"start": v(11.2, -10.67) * mm, "end": v(11.2, -10.46) * mm});
            skLineSegment(sketch, "E274", {"start": v(11.2, -10.46) * mm, "end": v(11.2, -10.26) * mm});
            skLineSegment(sketch, "E275", {"start": v(11.2, -10.26) * mm, "end": v(11.37, -9.67) * mm});
            skLineSegment(sketch, "E276", {"start": v(11.37, -9.67) * mm, "end": v(11.76, -9.15) * mm});
            skLineSegment(sketch, "E277", {"start": v(11.76, -9.15) * mm, "end": v(11.87, -9.06) * mm});
            skLineSegment(sketch, "E278", {"start": v(13.75, -6.42) * mm, "end": v(13.52, -6.42) * mm});
            skLineSegment(sketch, "E279", {"start": v(13.52, -6.42) * mm, "end": v(12.88, -6.67) * mm});
            skLineSegment(sketch, "E280", {"start": v(12.88, -6.67) * mm, "end": v(12.82, -6.72) * mm});
            skLineSegment(sketch, "E281", {"start": v(12.82, -6.72) * mm, "end": v(12.75, -6.76) * mm});
            skLineSegment(sketch, "E282", {"start": v(12.75, -6.76) * mm, "end": v(12.45, -7.28) * mm});
            skLineSegment(sketch, "E283", {"start": v(12.45, -7.28) * mm, "end": v(12.45, -7.45) * mm});
            skLineSegment(sketch, "E284", {"start": v(12.45, -7.45) * mm, "end": v(12.45, -7.62) * mm});
            skLineSegment(sketch, "E285", {"start": v(12.45, -7.62) * mm, "end": v(12.75, -8.06) * mm});
            skLineSegment(sketch, "E286", {"start": v(12.75, -8.06) * mm, "end": v(12.81, -8.1) * mm});
            skLineSegment(sketch, "E287", {"start": v(12.81, -8.1) * mm, "end": v(12.87, -8.15) * mm});
            skLineSegment(sketch, "E288", {"start": v(12.87, -8.15) * mm, "end": v(13.53, -8.36) * mm});
            skLineSegment(sketch, "E289", {"start": v(13.53, -8.36) * mm, "end": v(13.75, -8.36) * mm});
            skLineSegment(sketch, "E290", {"start": v(13.75, -8.36) * mm, "end": v(13.99, -8.36) * mm});
            skLineSegment(sketch, "E291", {"start": v(13.99, -8.36) * mm, "end": v(14.63, -8.15) * mm});
            skLineSegment(sketch, "E292", {"start": v(14.63, -8.15) * mm, "end": v(14.7, -8.1) * mm});
            skLineSegment(sketch, "E293", {"start": v(14.7, -8.1) * mm, "end": v(14.75, -8.06) * mm});
            skLineSegment(sketch, "E294", {"start": v(14.75, -8.06) * mm, "end": v(15.05, -7.6) * mm});
            skLineSegment(sketch, "E295", {"start": v(15.05, -7.6) * mm, "end": v(15.05, -7.44) * mm});
            skLineSegment(sketch, "E296", {"start": v(15.05, -7.44) * mm, "end": v(15.05, -7.26) * mm});
            skLineSegment(sketch, "E297", {"start": v(15.05, -7.26) * mm, "end": v(14.74, -6.76) * mm});
            skLineSegment(sketch, "E298", {"start": v(14.74, -6.76) * mm, "end": v(14.68, -6.71) * mm});
            skLineSegment(sketch, "E299", {"start": v(14.68, -6.71) * mm, "end": v(14.62, -6.66) * mm});
            skLineSegment(sketch, "E300", {"start": v(14.62, -6.66) * mm, "end": v(13.97, -6.42) * mm});
            skLineSegment(sketch, "E301", {"start": v(13.97, -6.42) * mm, "end": v(13.75, -6.42) * mm});
            skLineSegment(sketch, "E302", {"start": v(13.8, -9.08) * mm, "end": v(13.6, -9.08) * mm});
            skLineSegment(sketch, "E303", {"start": v(13.6, -9.08) * mm, "end": v(13.06, -9.17) * mm});
            skLineSegment(sketch, "E304", {"start": v(13.06, -9.17) * mm, "end": v(12.59, -9.39) * mm});
            skLineSegment(sketch, "E305", {"start": v(12.59, -9.39) * mm, "end": v(12.51, -9.45) * mm});
            skLineSegment(sketch, "E306", {"start": v(12.51, -9.45) * mm, "end": v(12.43, -9.5) * mm});
            skLineSegment(sketch, "E307", {"start": v(12.43, -9.5) * mm, "end": v(12.16, -9.88) * mm});
            skLineSegment(sketch, "E308", {"start": v(12.16, -9.88) * mm, "end": v(12.05, -10.31) * mm});
            skLineSegment(sketch, "E309", {"start": v(12.05, -10.31) * mm, "end": v(12.05, -10.45) * mm});
            skLineSegment(sketch, "E310", {"start": v(12.05, -10.45) * mm, "end": v(12.05, -10.6) * mm});
            skLineSegment(sketch, "E311", {"start": v(12.05, -10.6) * mm, "end": v(12.17, -11.01) * mm});
            skLineSegment(sketch, "E312", {"start": v(12.17, -11.01) * mm, "end": v(12.44, -11.4) * mm});
            skLineSegment(sketch, "E313", {"start": v(12.44, -11.4) * mm, "end": v(12.52, -11.46) * mm});
            skLineSegment(sketch, "E314", {"start": v(12.52, -11.46) * mm, "end": v(12.6, -11.52) * mm});
            skLineSegment(sketch, "E315", {"start": v(12.6, -11.52) * mm, "end": v(13.46, -11.84) * mm});
            skLineSegment(sketch, "E316", {"start": v(13.46, -11.84) * mm, "end": v(13.75, -11.84) * mm});
            skLineSegment(sketch, "E317", {"start": v(13.75, -11.84) * mm, "end": v(14.06, -11.84) * mm});
            skLineSegment(sketch, "E318", {"start": v(14.06, -11.84) * mm, "end": v(14.9, -11.52) * mm});
            skLineSegment(sketch, "E319", {"start": v(14.9, -11.52) * mm, "end": v(14.99, -11.46) * mm});
            skLineSegment(sketch, "E320", {"start": v(14.99, -11.46) * mm, "end": v(15.07, -11.4) * mm});
            skLineSegment(sketch, "E321", {"start": v(15.07, -11.4) * mm, "end": v(15.34, -11.01) * mm});
            skLineSegment(sketch, "E322", {"start": v(15.34, -11.01) * mm, "end": v(15.46, -10.6) * mm});
            skLineSegment(sketch, "E323", {"start": v(15.46, -10.6) * mm, "end": v(15.46, -10.45) * mm});
            skLineSegment(sketch, "E324", {"start": v(15.46, -10.45) * mm, "end": v(15.46, -10.31) * mm});
            skLineSegment(sketch, "E325", {"start": v(15.46, -10.31) * mm, "end": v(15.34, -9.9) * mm});
            skLineSegment(sketch, "E326", {"start": v(15.34, -9.9) * mm, "end": v(15.08, -9.52) * mm});
            skLineSegment(sketch, "E327", {"start": v(15.08, -9.52) * mm, "end": v(15, -9.46) * mm});
            skLineSegment(sketch, "E328", {"start": v(15, -9.46) * mm, "end": v(14.92, -9.4) * mm});
            skLineSegment(sketch, "E329", {"start": v(14.92, -9.4) * mm, "end": v(14.08, -9.08) * mm});
            skLineSegment(sketch, "E330", {"start": v(14.08, -9.08) * mm, "end": v(13.8, -9.08) * mm});
            skSolve(sketch);
        }
        {
            var Q0;
            Q0=qSketchRegion(id+"F3",true);
            var Q1;
            Q1=qSketchRegion(id+"F4",true);
            extrude(context, id + "F5", {"entities" : qUnion([Q0, Q1]), "depth" : -3 * mm});
        }
    });
